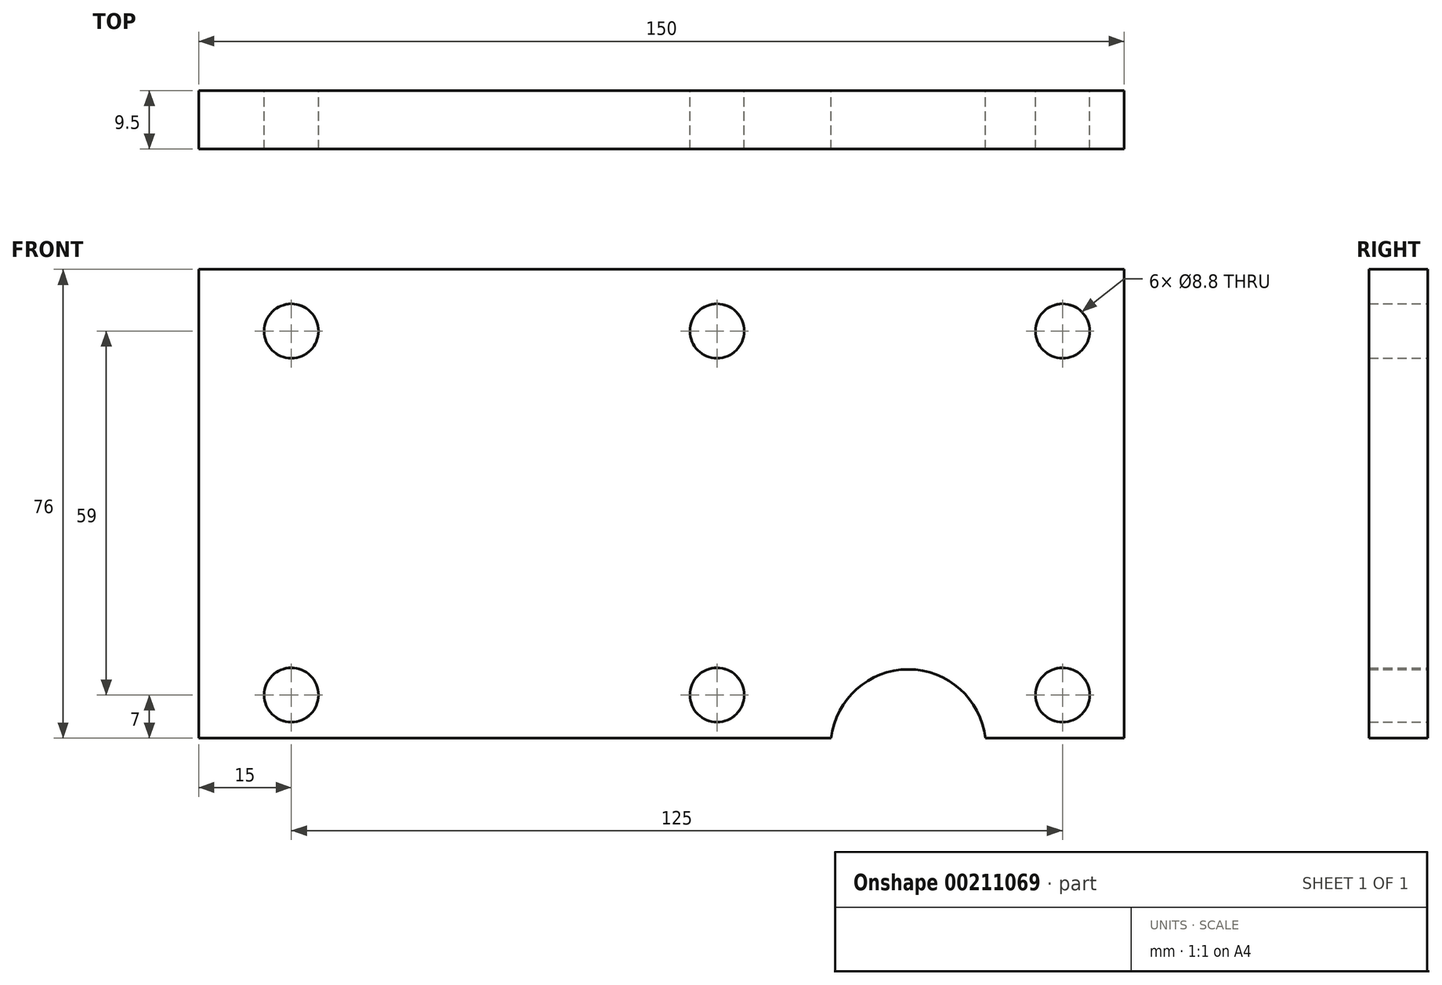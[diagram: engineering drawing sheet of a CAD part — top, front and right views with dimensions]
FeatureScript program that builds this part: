
annotation { "Feature Type Name" : "Feature", "Feature Type Description" : "" }
export const myFeature = defineFeature(function(context is Context, id is Id, definition is map)
    precondition{}
    {
        {
            var Q0;
            Q0=qCreatedBy(makeId("Front.planeOp"),FACE);
            var sketch = newSketch(context, id + "F0", { "sketchPlane" : qUnion([Q0])});
            skLineSegment(sketch, "E0.bottom", {"start": v(75, -38) * mm, "end": v(52.5, -38) * mm});
            skLineSegment(sketch, "E0.top", {"start": v(75, 38) * mm, "end": v(-75, 38) * mm});
            skLineSegment(sketch, "E0.left", {"start": v(75, -38) * mm, "end": v(75, 38) * mm});
            skLineSegment(sketch, "E0.right", {"start": v(-75, -38) * mm, "end": v(-75, 38) * mm});
            skPoint(sketch, "E0.middle", {"position": v(0, 0) * mm});
            skPoint(sketch, "E1", {"position": v(65, 28) * mm});
            skPoint(sketch, "E2", {"position": v(9, 28) * mm});
            skPoint(sketch, "E3", {"position": v(65, -31) * mm});
            skPoint(sketch, "E4", {"position": v(9, -31) * mm});
            skPoint(sketch, "E5", {"position": v(-60, 28) * mm});
            skPoint(sketch, "E6", {"position": v(-60, -31) * mm});
            skPoint(sketch, "E7", {"position": v(40, -38) * mm});
            skPoint(sketch, "E8", {"position": v(52.5, -38) * mm});
            skPoint(sketch, "E9", {"position": v(27.5, -38) * mm});
            skArc(sketch, "E10", {"start": v(52.5, -38) * mm, "mid": v(40, -26.85) * mm, "end": v(27.5, -38) * mm});
            skLineSegment(sketch, "E11.trimOffspring", {"start": v(27.5, -38) * mm, "end": v(-75, -38) * mm});
            skSolve(sketch);
        }
        {
            var Q0;
            Q0=makeQuery(id+"F0.imprint","IMPRINT",FACE,{"disambiguationData":[TD([[makeQuery(id+"F0.imprint","IMPRINT",EDGE,{"derivedFrom":sQuery(id+"F0.wireOp",EDGE,"E0.bottom")}),-1.0]])]});
            extrude(context, id + "F1", {"entities" : qUnion([Q0]), "depth" : 9.5 * mm});
        }
        {
            var Q0;
            Q0=qCreatedBy(makeId("Front.planeOp"),FACE);
            var sketch = newSketch(context, id + "F2", { "sketchPlane" : qUnion([Q0])});
            skPoint(sketch, "E12", {"position": v(65, 28) * mm});
            skPoint(sketch, "E13", {"position": v(65, -31) * mm});
            skPoint(sketch, "E14", {"position": v(9, 28) * mm});
            skPoint(sketch, "E15", {"position": v(9, -31) * mm});
            skPoint(sketch, "E16", {"position": v(-60, 28) * mm});
            skPoint(sketch, "E17", {"position": v(-60, -31) * mm});
            skSolve(sketch);
        }
        {
            var Q0;
            Q0=sQuery(id+"F2.wireOp",VERTEX,"E16");
            var Q1;
            Q1=sQuery(id+"F2.wireOp",VERTEX,"E12");
            var Q2;
            Q2=sQuery(id+"F2.wireOp",VERTEX,"E15");
            var Q3;
            Q3=sQuery(id+"F2.wireOp",VERTEX,"E17");
            var Q4;
            Q4=sQuery(id+"F2.wireOp",VERTEX,"E13");
            var Q5;
            Q5=sQuery(id+"F2.wireOp",VERTEX,"E14");
            var Q6;
            Q6=makeQuery(id+"F1.opExtrude","SWEPT_BODY",BODY,{"disambiguationData":[OSD([sQuery(id+"F0.wireOp",EDGE,"E0.bottom"),sQuery(id+"F0.wireOp",EDGE,"E0.top"),sQuery(id+"F0.wireOp",EDGE,"E0.left"),sQuery(id+"F0.wireOp",EDGE,"E0.right"),sQuery(id+"F0.wireOp",EDGE,"E10"),sQuery(id+"F0.wireOp",EDGE,"E11.trimOffspring")])]});
            hole(context, id + "F3", {"style" : HoleStyle.C_SINK, "endStyle" : HoleEndStyle.THROUGH, "oppositeDirection" : true, "holeDiameter" : 8.8 * mm, "cSinkDiameter" : 9 * mm, "cSinkAngle" : 90 * degree, "startFromSketch" : true, "locations" : qUnion([Q0, Q1, Q2, Q3, Q4, Q5]), "scope" : qUnion([Q6]), "isTappedThrough" : true});
        }
    });
